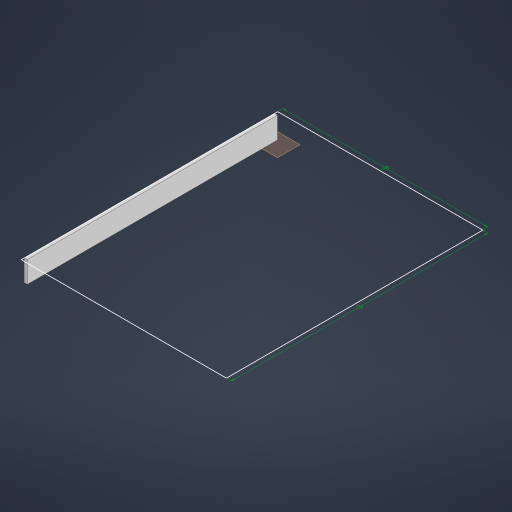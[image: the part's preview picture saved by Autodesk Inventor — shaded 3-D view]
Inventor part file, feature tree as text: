
AUTODESK INVENTOR PART (.ipt)
format: ipt  version: 2023 (Build 270158000, 158)  size: 248,832 bytes
history: native  units: mm
features: extrude x7, sketch x5, other x2, shell x1, plane x1
ambient origin geometry x8: Origin, YZ Plane, XZ Plane, XY Plane, X Axis, Y Axis, Z Axis, Center Point
bodies: Body1 (feature_tree)
feature tree (16):
  other  "block"
  extrude  "ext_block"  Depth=250.0mm
  shell  "Shell2"  Thickness=12.0mm
  extrude  "holes"  Depth=25.0mm
  extrude  "pwr_button_hole"  Depth=17.0mm
  plane  "Work Plane1"
  extrude  "back_cover_cut"  Depth=75.0mm
  extrude  "Extrusion8"  Depth=3.0mm
  extrude  "Extrusion9"  Depth=3.0mm
  extrude  "Extrusion10"  Depth=3.0mm
  other  "lines_base"
  sketch  "Sketch4"  dims[d0=200.0mm d1=250.0mm d2=12.0mm]
  sketch  "Sketch5"  dims[d3=12.0mm d4=25.0mm]
  sketch  "Sketch10"  dims[d5=17.0mm d6=17.0mm]
  sketch  "Sketch11"  dims[d7=25.0mm d8=75.0mm]
  sketch  "Sketch12"  dims[d9=80.0mm d10=65.0mm d11=60.0mm d12=6.0mm d13=84.0mm d14=90.0deg d15=25.0mm d16=125.0mm d17=70.0mm d19=14.0mm d20=10.0mm d22=10.0mm d24=5.0mm d25=10.0mm d26=65.0mm d27=95.0mm d31=200.0mm d32=250.0mm d35=24.0mm d36=0.0mm d37=3.0mm d38=24.0mm d39=0.0mm d40=19.0mm d41=13.0mm d42=4.0mm d43=12.0mm d44=24.0mm d45=0.0mm d49=0.0mm d50=0.0mm d62=10.0mm d63=0.0mm d64=10.0mm d65=0.0mm d66=0.0mm d67=0.0mm d33=0.5mm d34=0.872665mm]
